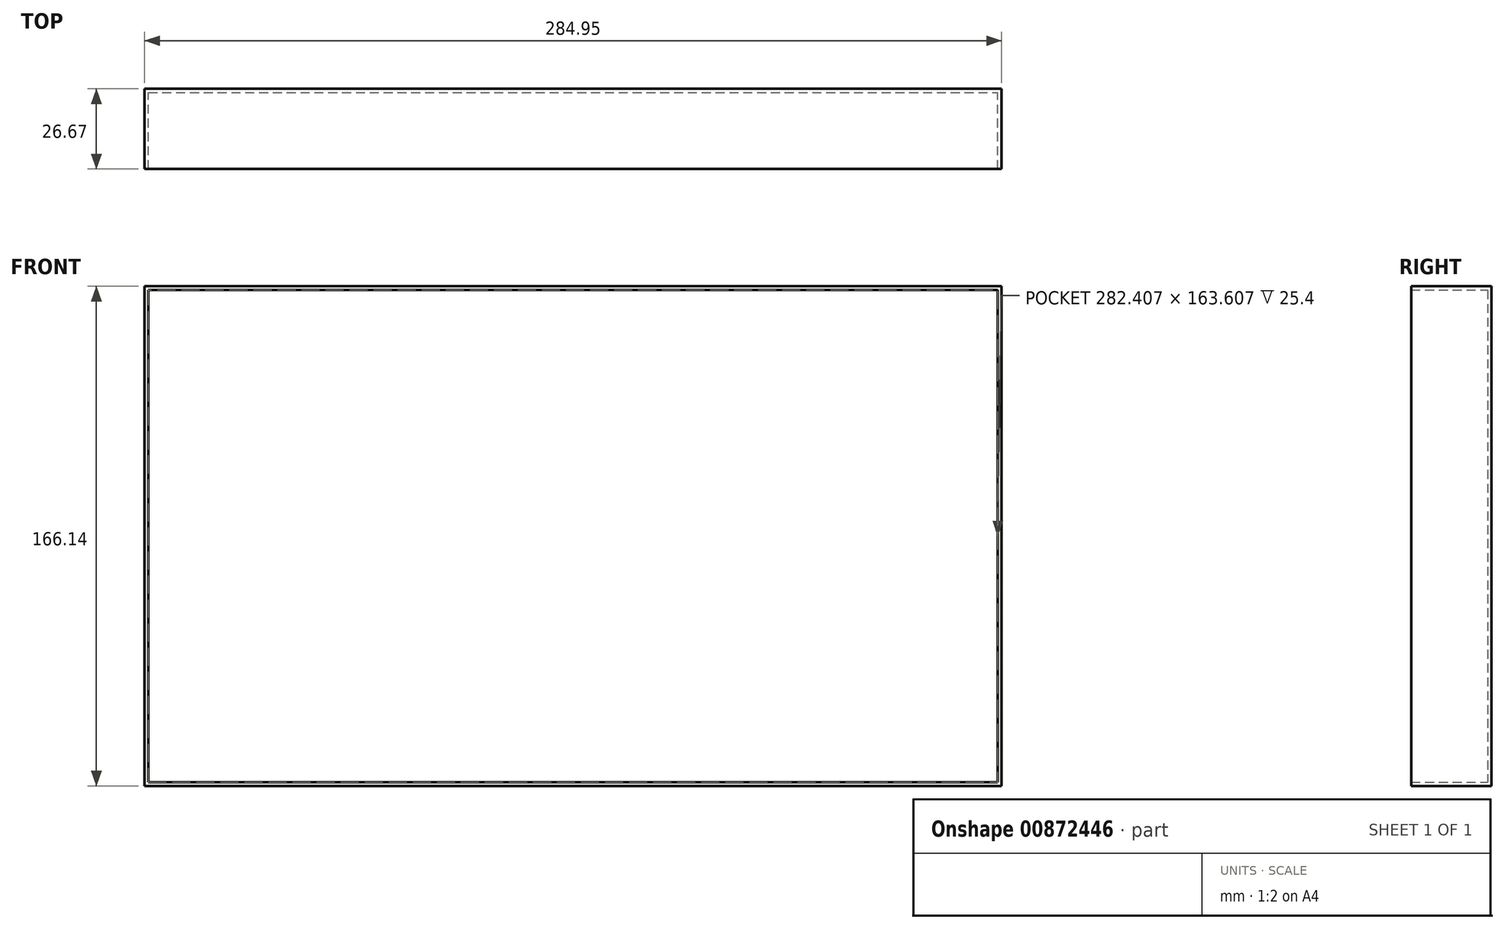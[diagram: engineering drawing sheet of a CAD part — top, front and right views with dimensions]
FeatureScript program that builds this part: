
annotation { "Feature Type Name" : "Feature", "Feature Type Description" : "" }
export const myFeature = defineFeature(function(context is Context, id is Id, definition is map)
    precondition{}
    {
        {
            var Q0;
            Q0=qCreatedBy(makeId("Front.planeOp"),FACE);
            var sketch = newSketch(context, id + "F0", { "sketchPlane" : qUnion([Q0])});
            skLineSegment(sketch, "E0.bottom", {"start": v(-152.5, 81.4) * mm, "end": v(129.9, 81.4) * mm});
            skLineSegment(sketch, "E0.top", {"start": v(-152.5, -82.21) * mm, "end": v(129.9, -82.21) * mm});
            skLineSegment(sketch, "E0.left", {"start": v(-152.5, 81.4) * mm, "end": v(-152.5, -82.21) * mm});
            skLineSegment(sketch, "E0.right", {"start": v(129.9, 81.4) * mm, "end": v(129.9, -82.21) * mm});
            skSolve(sketch);
        }
        {
            var Q0;
            Q0=makeQuery(id+"F0.imprint","IMPRINT",FACE,{"disambiguationData":[TD([[makeQuery(id+"F0.imprint","IMPRINT",EDGE,{"derivedFrom":sQuery(id+"F0.wireOp",EDGE,"E0.bottom")}),-1.0]])]});
            extrude(context, id + "F1", {"entities" : qUnion([Q0]), "endBound" : BoundingType.SYMMETRIC, "depth" : 25.4 * mm, "offsetDistance" : 25.4 * mm});
        }
        {
            var Q0;
            Q0=makeQuery(id+"F1.opExtrude","CAP_FACE",FACE,{"disambiguationData":[OSD([sQuery(id+"F0.wireOp",EDGE,"E0.bottom"),sQuery(id+"F0.wireOp",EDGE,"E0.top"),sQuery(id+"F0.wireOp",EDGE,"E0.left"),sQuery(id+"F0.wireOp",EDGE,"E0.right")])],"isStart":false});
            shell(context, id + "F2", {"entities" : qUnion([Q0]), "thickness" : 1.27 * mm, "oppositeDirection" : true});
        }
    });
